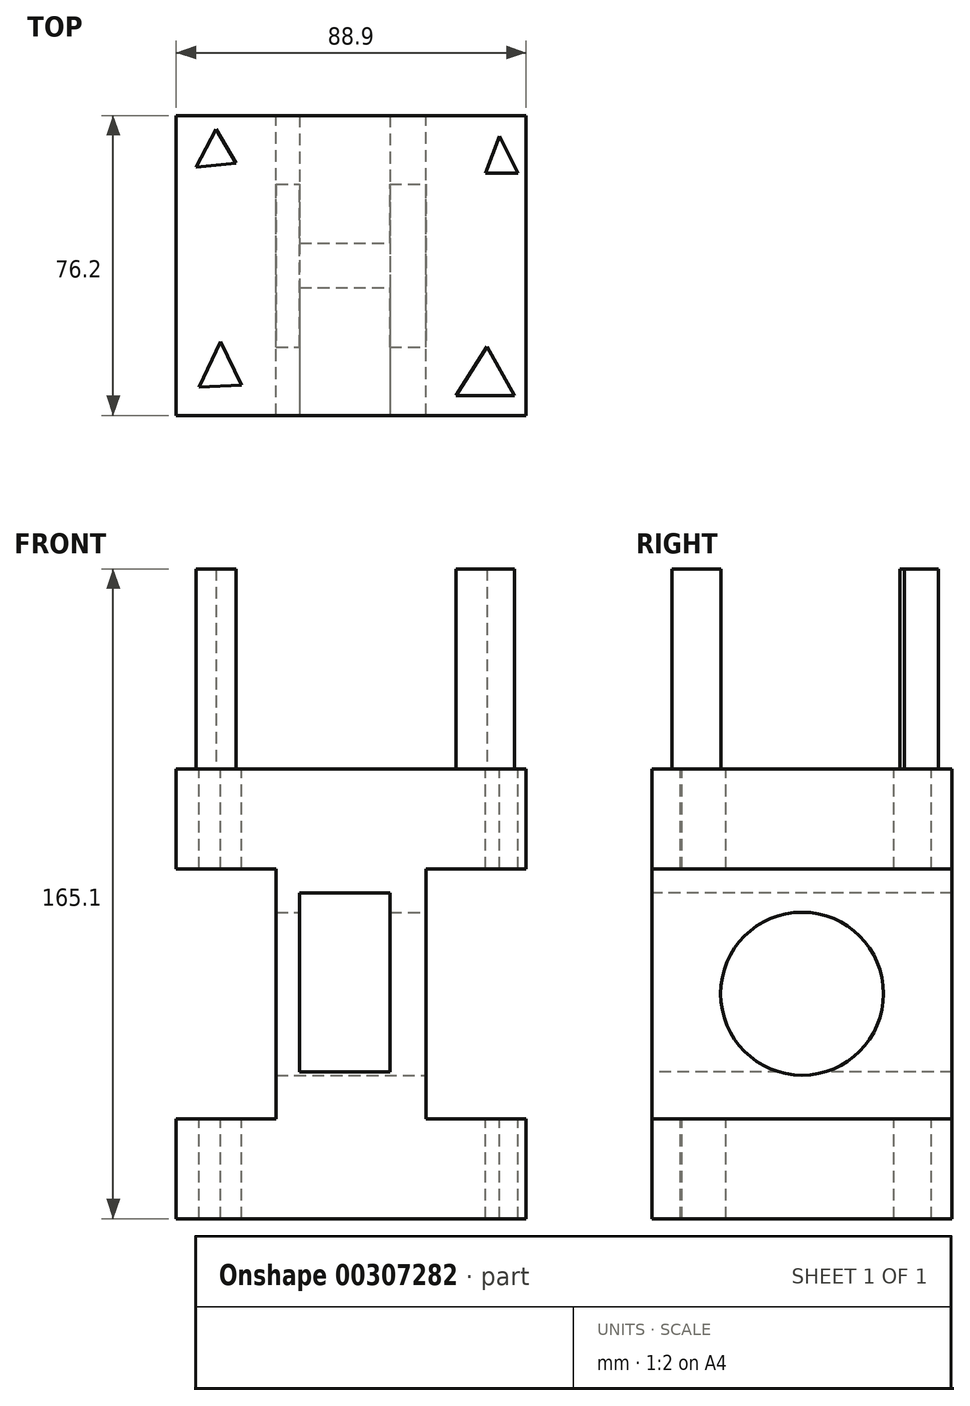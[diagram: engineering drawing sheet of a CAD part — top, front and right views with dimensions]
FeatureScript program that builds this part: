
annotation { "Feature Type Name" : "Feature", "Feature Type Description" : "" }
export const myFeature = defineFeature(function(context is Context, id is Id, definition is map)
    precondition{}
    {
        {
            var Q0;
            Q0=qCreatedBy(makeId("Front.planeOp"),FACE);
            var sketch = newSketch(context, id + "F0", { "sketchPlane" : qUnion([Q0])});
            skLineSegment(sketch, "E0", {"start": v(-40.36, -54.6) * mm, "end": v(48.54, -54.6) * mm});
            skLineSegment(sketch, "E1", {"start": v(48.54, -54.6) * mm, "end": v(48.54, -29.2) * mm});
            skLineSegment(sketch, "E2", {"start": v(48.54, -29.2) * mm, "end": v(23.14, -29.2) * mm});
            skLineSegment(sketch, "E3", {"start": v(23.14, -29.2) * mm, "end": v(23.14, 34.3) * mm});
            skLineSegment(sketch, "E4", {"start": v(23.14, 34.3) * mm, "end": v(48.54, 34.3) * mm});
            skLineSegment(sketch, "E5", {"start": v(48.54, 34.3) * mm, "end": v(48.54, 59.7) * mm});
            skLineSegment(sketch, "E6", {"start": v(48.54, 59.7) * mm, "end": v(-40.36, 59.7) * mm});
            skLineSegment(sketch, "E7", {"start": v(-40.36, 59.7) * mm, "end": v(-40.36, 34.3) * mm});
            skLineSegment(sketch, "E8", {"start": v(-14.96, 34.3) * mm, "end": v(-40.36, 34.3) * mm});
            skLineSegment(sketch, "E9", {"start": v(-14.96, 34.3) * mm, "end": v(-14.96, -29.2) * mm});
            skLineSegment(sketch, "E10", {"start": v(-14.96, -29.2) * mm, "end": v(-40.36, -29.2) * mm});
            skLineSegment(sketch, "E11", {"start": v(-40.36, -29.2) * mm, "end": v(-40.36, -54.6) * mm});
            skSolve(sketch);
        }
        {
            var Q0;
            Q0=makeQuery(id+"F0.imprint","IMPRINT",FACE,{"disambiguationData":[TD([[makeQuery(id+"F0.imprint","IMPRINT",EDGE,{"derivedFrom":sQuery(id+"F0.wireOp",EDGE,"E0")}),1.0]])]});
            extrude(context, id + "F1", {"entities" : qUnion([Q0]), "depth" : 76.2 * mm});
        }
        {
            var Q0;
            Q0=makeQuery(id+"F1.opExtrude","SWEPT_FACE",FACE,{"disambiguationData":[OSD([sQuery(id+"F0.wireOp",EDGE,"E3")])]});
            var sketch = newSketch(context, id + "F2", { "sketchPlane" : qUnion([Q0])});
            skCircle(sketch, "E12", {"center": v(-38.1, 2.55) * mm, "radius": 20.7 * mm});
            skPoint(sketch, "E12.centerSnap0", {"position": v(-38.1, 34.3) * mm});
            skPoint(sketch, "E12.centerSnap1", {"position": v(-76.2, 2.55) * mm});
            skSolve(sketch);
        }
        {
            var Q0;
            Q0=makeQuery(id+"F2.imprint","IMPRINT",FACE,{"disambiguationData":[TD([[makeQuery(id+"F2.imprint","IMPRINT",EDGE,{"derivedFrom":sQuery(id+"F2.wireOp",EDGE,"E12")}),1.0]])]});
            extrude(context, id + "F3", {"entities" : qUnion([Q0]), "operationType" : NewBodyOperationType.REMOVE, "endBound" : BoundingType.THROUGH_ALL, "oppositeDirection" : true, "depth" : 25.4 * mm});
        }
        {
            var Q0;
            Q0=makeQuery(id+"F1.opExtrude","SWEPT_FACE",FACE,{"disambiguationData":[OSD([sQuery(id+"F0.wireOp",EDGE,"E6")])]});
            var sketch = newSketch(context, id + "F4", { "sketchPlane" : qUnion([Q0])});
            skLineSegment(sketch, "E13", {"start": v(30.2, -71.97) * mm, "end": v(38.65, -58.67) * mm});
            skLineSegment(sketch, "E14", {"start": v(38.65, -58.67) * mm, "end": v(45.61, -71.13) * mm});
            skLineSegment(sketch, "E15", {"start": v(45.61, -71.13) * mm, "end": v(30.74, -71.13) * mm});
            skSolve(sketch);
        }
        {
            var Q0;
            {var subQ0=sQuery(id+"F4.wireOp",EDGE,"E14");Q0=makeQuery(id+"F4.imprint","IMPRINT",FACE,{"disambiguationData":[TD([[makeQuery(id+"F4.imprint","IMPRINT",EDGE,{"derivedFrom":subQ0}),-1.0]])]});}
            extrude(context, id + "F5", {"entities" : qUnion([Q0]), "operationType" : NewBodyOperationType.ADD, "depth" : 50.8 * mm});
        }
        {
            var Q0;
            Q0=makeQuery(id+"F1.opExtrude","SWEPT_FACE",FACE,{"disambiguationData":[OSD([sQuery(id+"F0.wireOp",EDGE,"E6")])]});
            var sketch = newSketch(context, id + "F6", { "sketchPlane" : qUnion([Q0])});
            skLineSegment(sketch, "E16", {"start": v(-34.55, -69) * mm, "end": v(-29.13, -57.5) * mm});
            skLineSegment(sketch, "E17", {"start": v(-29.13, -57.5) * mm, "end": v(-23.7, -68.57) * mm});
            skLineSegment(sketch, "E18", {"start": v(-23.7, -68.57) * mm, "end": v(-34.55, -69) * mm});
            skSolve(sketch);
        }
        {
            var Q0;
            Q0=makeQuery(id+"F6.imprint","IMPRINT",FACE,{"disambiguationData":[TD([[makeQuery(id+"F6.imprint","IMPRINT",EDGE,{"derivedFrom":sQuery(id+"F6.wireOp",EDGE,"E16")}),-1.0]])]});
            extrude(context, id + "F7", {"entities" : qUnion([Q0]), "operationType" : NewBodyOperationType.REMOVE, "endBound" : BoundingType.THROUGH_ALL, "oppositeDirection" : true, "depth" : 25.4 * mm});
        }
        {
            var Q0;
            Q0=makeQuery(id+"F1.opExtrude","SWEPT_FACE",FACE,{"disambiguationData":[OSD([sQuery(id+"F0.wireOp",EDGE,"E6")])]});
            var sketch = newSketch(context, id + "F8", { "sketchPlane" : qUnion([Q0])});
            skLineSegment(sketch, "E19", {"start": v(-35.32, -13.2) * mm, "end": v(-30.21, -3.43) * mm});
            skLineSegment(sketch, "E20", {"start": v(-30.21, -3.43) * mm, "end": v(-25.1, -12.15) * mm});
            skLineSegment(sketch, "E21", {"start": v(-25.1, -12.15) * mm, "end": v(-35.32, -13.2) * mm});
            skSolve(sketch);
        }
        {
            var Q0;
            Q0=makeQuery(id+"F8.imprint","IMPRINT",FACE,{"disambiguationData":[TD([[makeQuery(id+"F8.imprint","IMPRINT",EDGE,{"derivedFrom":sQuery(id+"F8.wireOp",EDGE,"E19")}),-1.0]])]});
            extrude(context, id + "F9", {"entities" : qUnion([Q0]), "operationType" : NewBodyOperationType.ADD, "depth" : 50.8 * mm});
        }
        {
            var Q0;
            Q0=makeQuery(id+"F1.opExtrude","SWEPT_FACE",FACE,{"disambiguationData":[OSD([sQuery(id+"F0.wireOp",EDGE,"E6")])]});
            var sketch = newSketch(context, id + "F10", { "sketchPlane" : qUnion([Q0])});
            skLineSegment(sketch, "E22", {"start": v(38.17, -14.7) * mm, "end": v(46.43, -14.7) * mm});
            skLineSegment(sketch, "E23", {"start": v(46.43, -14.7) * mm, "end": v(41.77, -5.23) * mm});
            skLineSegment(sketch, "E24", {"start": v(41.77, -5.23) * mm, "end": v(38.17, -14.7) * mm});
            skSolve(sketch);
        }
        {
            var Q0;
            Q0=makeQuery(id+"F10.imprint","IMPRINT",FACE,{"disambiguationData":[TD([[makeQuery(id+"F10.imprint","IMPRINT",EDGE,{"derivedFrom":sQuery(id+"F10.wireOp",EDGE,"E22")}),1.0]])]});
            extrude(context, id + "F11", {"entities" : qUnion([Q0]), "operationType" : NewBodyOperationType.REMOVE, "endBound" : BoundingType.THROUGH_ALL, "oppositeDirection" : true, "depth" : 25.4 * mm});
        }
        {
            var Q0;
            Q0=makeQuery(id+"F1.opExtrude","CAP_FACE",FACE,{"disambiguationData":[OSD([sQuery(id+"F0.wireOp",EDGE,"E0"),sQuery(id+"F0.wireOp",EDGE,"E1"),sQuery(id+"F0.wireOp",EDGE,"E2"),sQuery(id+"F0.wireOp",EDGE,"E3"),sQuery(id+"F0.wireOp",EDGE,"E4"),sQuery(id+"F0.wireOp",EDGE,"E5"),sQuery(id+"F0.wireOp",EDGE,"E6"),sQuery(id+"F0.wireOp",EDGE,"E7"),sQuery(id+"F0.wireOp",EDGE,"E8"),sQuery(id+"F0.wireOp",EDGE,"E9"),sQuery(id+"F0.wireOp",EDGE,"E10"),sQuery(id+"F0.wireOp",EDGE,"E11")])],"isStart":false});
            var sketch = newSketch(context, id + "F12", { "sketchPlane" : qUnion([Q0])});
            skLineSegment(sketch, "E25", {"start": v(-9, 28.14) * mm, "end": v(-9, -17.35) * mm});
            skLineSegment(sketch, "E26", {"start": v(-9, -17.35) * mm, "end": v(13.94, -17.35) * mm});
            skLineSegment(sketch, "E27", {"start": v(13.94, -17.35) * mm, "end": v(13.94, 28.14) * mm});
            skLineSegment(sketch, "E28", {"start": v(13.94, 28.14) * mm, "end": v(-9, 28.14) * mm});
            skSolve(sketch);
        }
        {
            var Q0;
            Q0=makeQuery(id+"F12.imprint","IMPRINT",FACE,{"disambiguationData":[TD([[makeQuery(id+"F12.imprint","IMPRINT",EDGE,{"derivedFrom":sQuery(id+"F12.wireOp",EDGE,"E25")}),1.0]])]});
            extrude(context, id + "F13", {"entities" : qUnion([Q0]), "operationType" : NewBodyOperationType.REMOVE, "endBound" : BoundingType.THROUGH_ALL, "oppositeDirection" : true, "depth" : 25.4 * mm});
        }
    });
